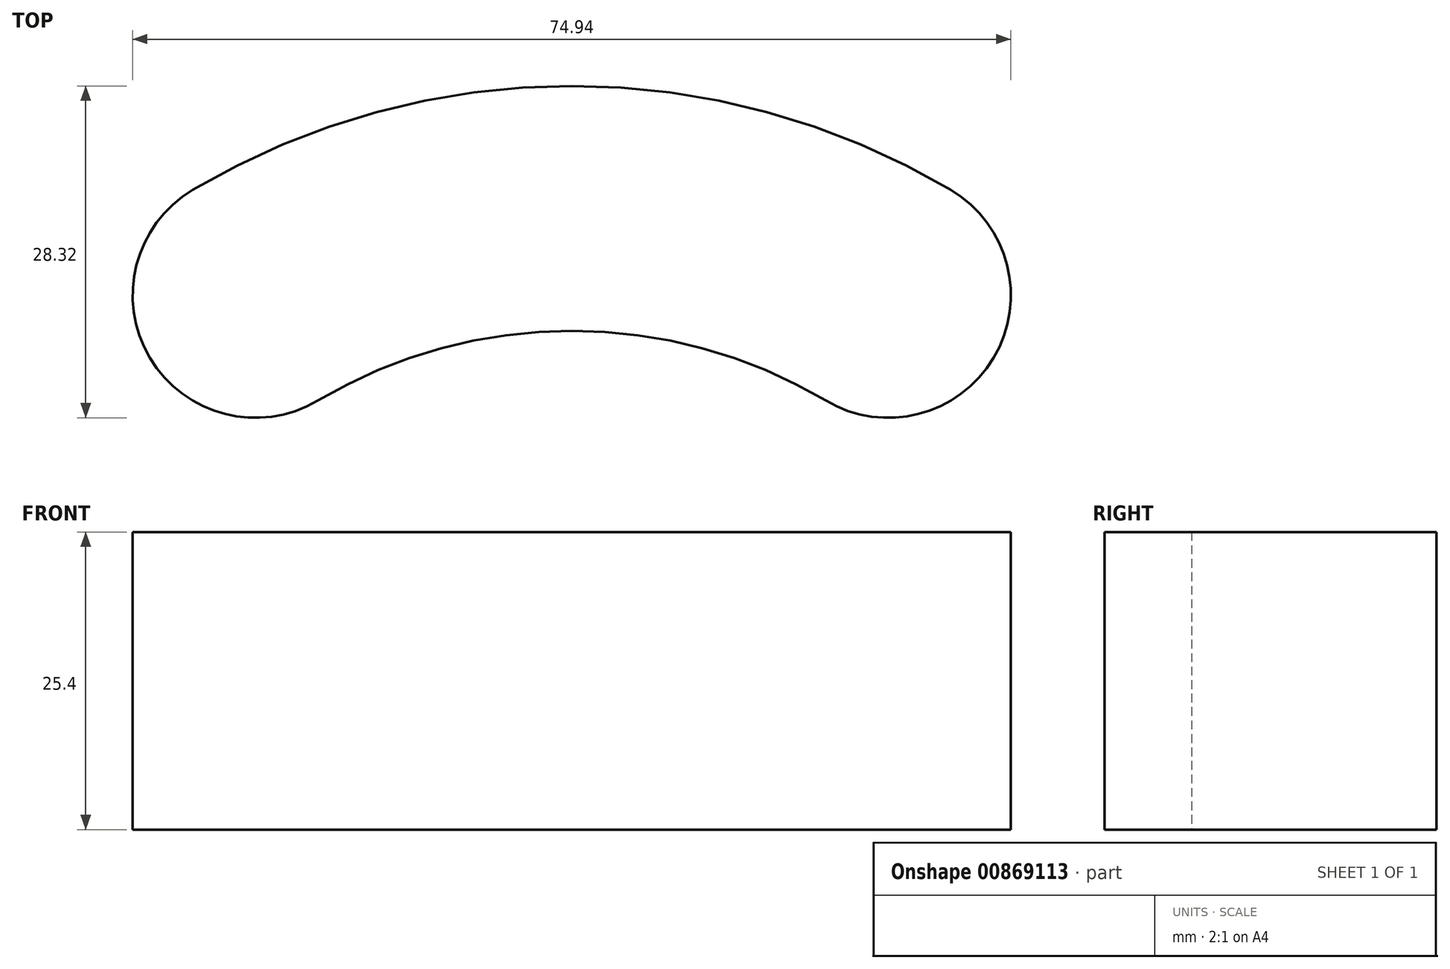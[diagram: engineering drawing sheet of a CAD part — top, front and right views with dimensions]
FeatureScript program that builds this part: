
annotation { "Feature Type Name" : "Feature", "Feature Type Description" : "" }
export const myFeature = defineFeature(function(context is Context, id is Id, definition is map)
    precondition{}
    {
        {
            var Q0;
            Q0=qCreatedBy(makeId("Top.planeOp"),FACE);
            var sketch = newSketch(context, id + "F0", { "sketchPlane" : qUnion([Q0])});
            skArc(sketch, "E0", {"start": v(-32.35, 8.99) * mm, "mid": v(-36, -5.34) * mm, "end": v(-21.68, -8.99) * mm});
            skArc(sketch, "E1.MirrorC", {"start": v(32.35, 8.99) * mm, "mid": v(36, -5.34) * mm, "end": v(21.68, -8.99) * mm});
            skArc(sketch, "E2", {"start": v(21.68, -8.99) * mm, "mid": v(0, -3.04) * mm, "end": v(-21.68, -8.99) * mm});
            skArc(sketch, "E3", {"start": v(32.35, 8.99) * mm, "mid": v(0, 17.87) * mm, "end": v(-32.35, 8.99) * mm});
            skSolve(sketch);
        }
        {
            var Q0;
            Q0=makeQuery(id+"F0.imprint","IMPRINT",FACE,{"disambiguationData":[TD([[makeQuery(id+"F0.imprint","IMPRINT",EDGE,{"derivedFrom":sQuery(id+"F0.wireOp",EDGE,"E0")}),1.0]])]});
            extrude(context, id + "F1", {"entities" : qUnion([Q0]), "depth" : 25.4 * mm, "offsetDistance" : 25.4 * mm});
        }
    });
